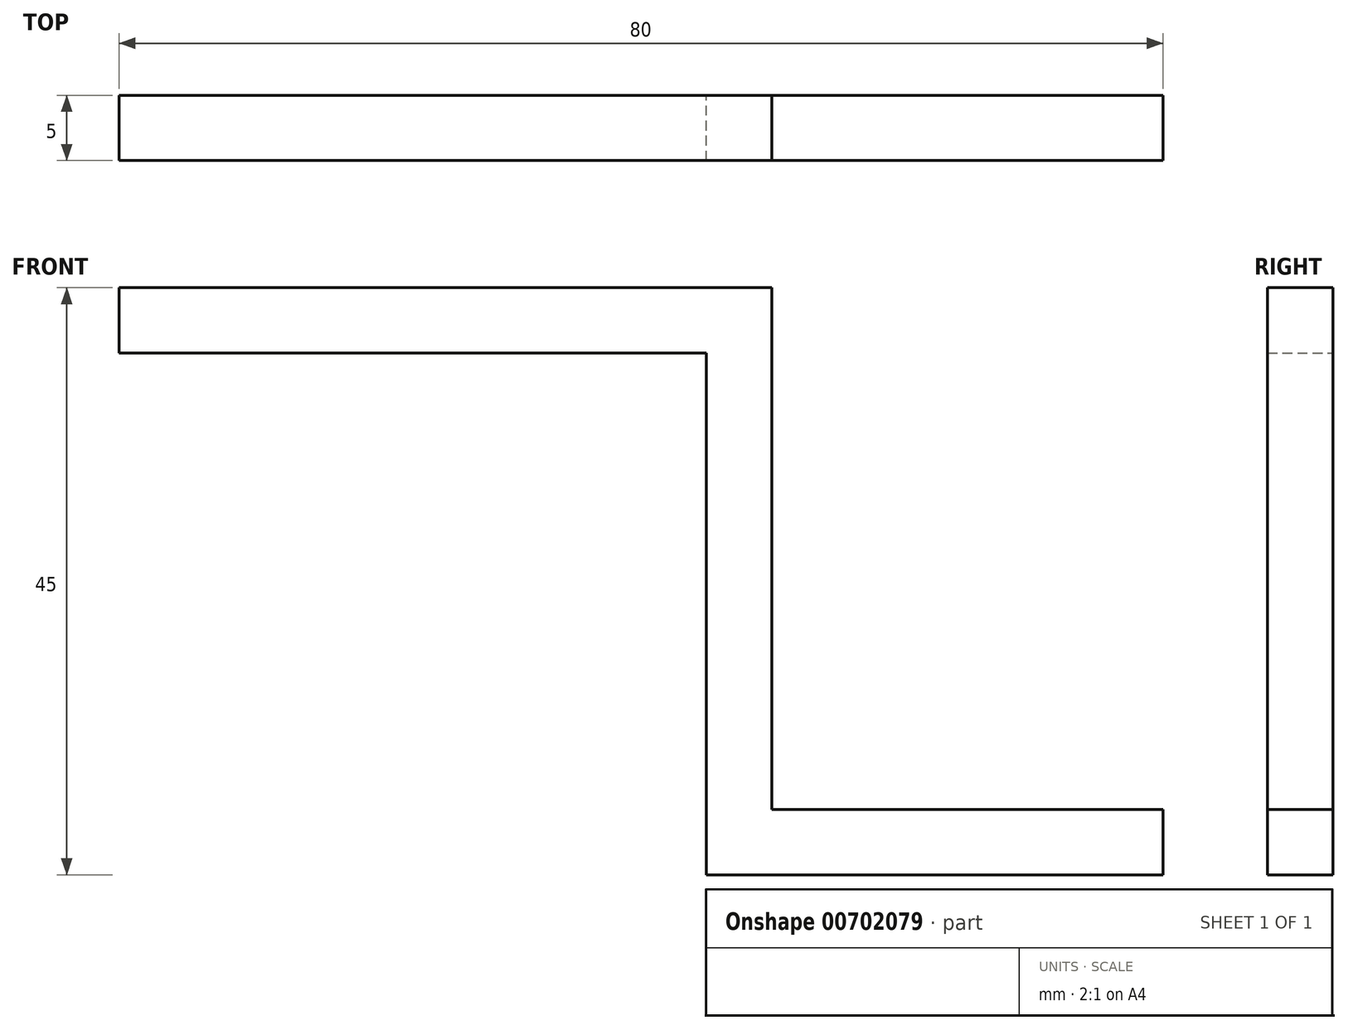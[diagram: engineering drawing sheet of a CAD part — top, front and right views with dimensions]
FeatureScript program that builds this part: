
annotation { "Feature Type Name" : "Feature", "Feature Type Description" : "" }
export const myFeature = defineFeature(function(context is Context, id is Id, definition is map)
    precondition{}
    {
        {
            var Q0;
            Q0=qCreatedBy(makeId("Front.planeOp"),FACE);
            var sketch = newSketch(context, id + "F0", { "sketchPlane" : qUnion([Q0])});
            skLineSegment(sketch, "E0.bottom", {"start": v(-37.46, 50.7) * mm, "end": v(7.54, 50.7) * mm});
            skLineSegment(sketch, "E0.top", {"start": v(-37.46, 45.7) * mm, "end": v(7.54, 45.7) * mm});
            skLineSegment(sketch, "E0.left", {"start": v(-37.46, 50.7) * mm, "end": v(-37.46, 45.7) * mm});
            skLineSegment(sketch, "E0.right", {"start": v(7.54, 50.7) * mm, "end": v(7.54, 50.7) * mm});
            skLineSegment(sketch, "E1.bottom", {"start": v(7.54, 50.7) * mm, "end": v(12.54, 50.7) * mm});
            skLineSegment(sketch, "E1.top", {"start": v(7.54, 5.7) * mm, "end": v(12.54, 5.7) * mm});
            skLineSegment(sketch, "E1.right", {"start": v(12.54, 50.7) * mm, "end": v(12.54, 10.7) * mm});
            skLineSegment(sketch, "E2.bottom", {"start": v(27.54, 5.7) * mm, "end": v(12.54, 5.7) * mm});
            skLineSegment(sketch, "E2.top", {"start": v(27.54, 10.7) * mm, "end": v(12.54, 10.7) * mm});
            skLineSegment(sketch, "E2.left", {"start": v(27.54, 5.7) * mm, "end": v(27.54, 10.7) * mm});
            skLineSegment(sketch, "E3", {"start": v(12.54, 5.7) * mm, "end": v(12.54, 5.7) * mm});
            skLineSegment(sketch, "E4", {"start": v(7.54, 45.7) * mm, "end": v(7.54, 45.7) * mm});
            skLineSegment(sketch, "E5", {"start": v(7.54, 45.7) * mm, "end": v(7.54, 5.7) * mm});
            skPoint(sketch, "E6.positionSnap0", {"position": v(27.54, 8.2) * mm});
            skPoint(sketch, "E7", {"position": v(20.04, 10.7) * mm});
            skSolve(sketch);
        }
        {
            var Q0;
            Q0 = qSketchRegion(id + "F0", true);
            extrude(context, id + "F1", {"entities" : qUnion([Q0]), "depth" : 25 * mm, "offsetDistance" : 25 * mm});
        }
        {
            var Q0;
            Q0=makeQuery(id+"F1.opExtrude","CAP_FACE",FACE,{"disambiguationData":[OSD([sQuery(id+"F0.wireOp",EDGE,"E0.bottom"),sQuery(id+"F0.wireOp",EDGE,"E0.top"),sQuery(id+"F0.wireOp",EDGE,"E0.left"),sQuery(id+"F0.wireOp",EDGE,"E1.bottom"),sQuery(id+"F0.wireOp",EDGE,"E1.top"),sQuery(id+"F0.wireOp",EDGE,"E1.right"),sQuery(id+"F0.wireOp",EDGE,"E2.bottom"),sQuery(id+"F0.wireOp",EDGE,"E2.top"),sQuery(id+"F0.wireOp",EDGE,"E2.left"),sQuery(id+"F0.wireOp",EDGE,"E5")])],"isStart":true});
            extrude(context, id + "F2", {"entities" : qUnion([Q0]), "operationType" : NewBodyOperationType.REMOVE, "oppositeDirection" : true, "depth" : 20 * mm, "offsetDistance" : 25 * mm});
        }
        {
            var Q0;
            Q0=makeQuery(id+"F1.opExtrude","SWEPT_FACE",FACE,{"disambiguationData":[OSD([sQuery(id+"F0.wireOp",EDGE,"E2.left")])]});
            extrude(context, id + "F3", {"entities" : qUnion([Q0]), "operationType" : NewBodyOperationType.ADD, "depth" : 15 * mm, "offsetDistance" : 25 * mm});
        }
    });
